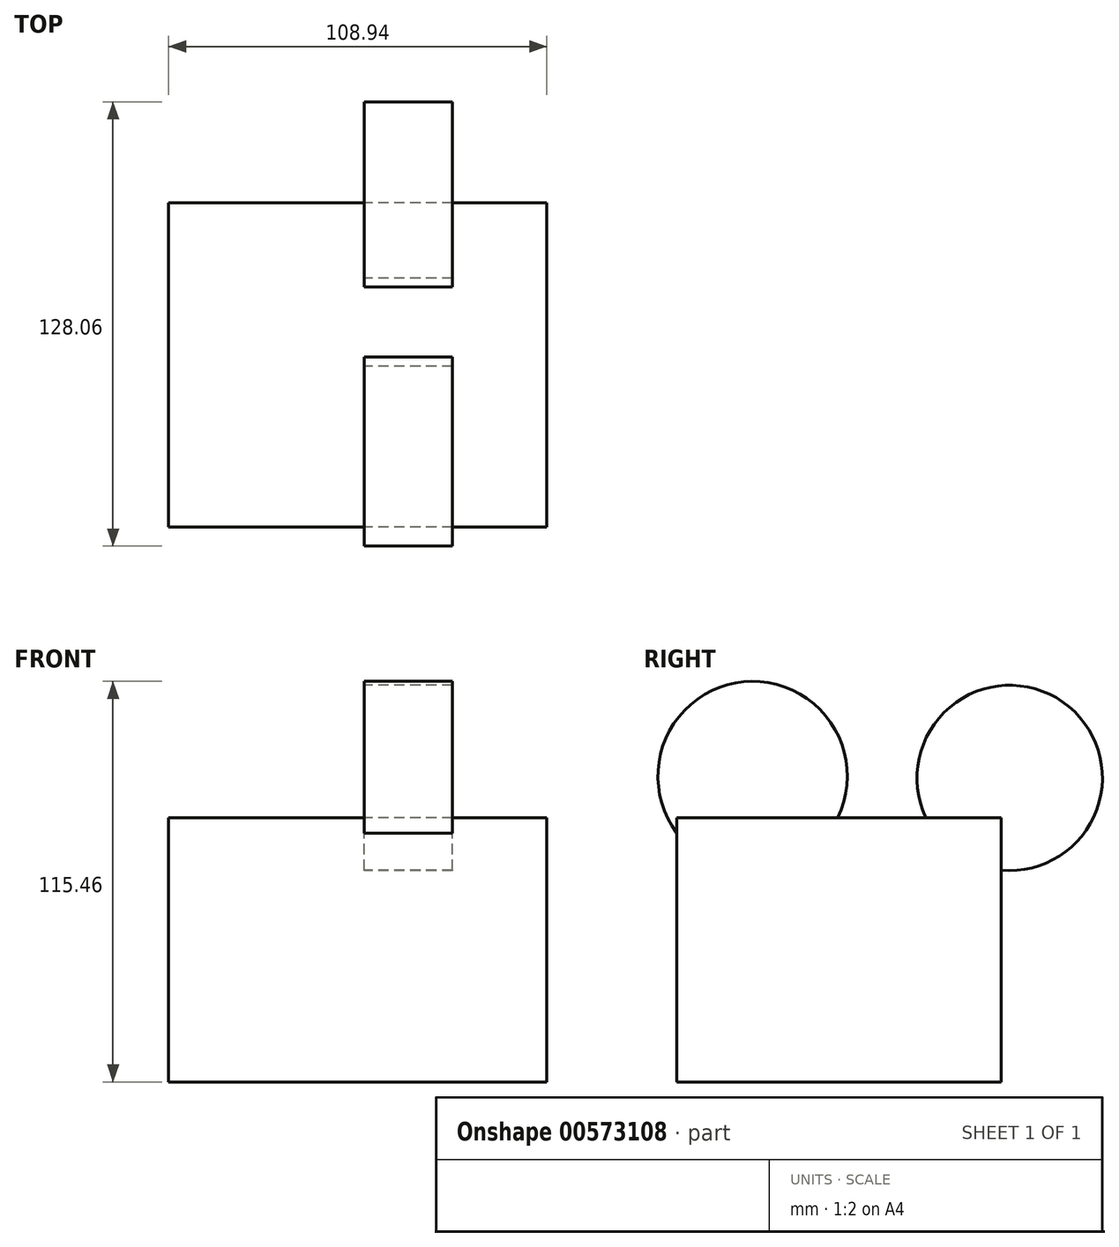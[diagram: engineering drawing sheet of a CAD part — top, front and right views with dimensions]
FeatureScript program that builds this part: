
annotation { "Feature Type Name" : "Feature", "Feature Type Description" : "" }
export const myFeature = defineFeature(function(context is Context, id is Id, definition is map)
    precondition{}
    {
        {
            var Q0;
            Q0=qCreatedBy(makeId("Top.planeOp"),FACE);
            var sketch = newSketch(context, id + "F0", { "sketchPlane" : qUnion([Q0])});
            skLineSegment(sketch, "E0.bottom", {"start": v(-51.08, 45.67) * mm, "end": v(59.45, 45.67) * mm});
            skLineSegment(sketch, "E0.top", {"start": v(-51.08, -51.44) * mm, "end": v(59.45, -51.44) * mm});
            skLineSegment(sketch, "E0.left", {"start": v(-51.08, 45.67) * mm, "end": v(-51.08, -51.44) * mm});
            skLineSegment(sketch, "E0.right", {"start": v(59.45, 45.67) * mm, "end": v(59.45, -51.44) * mm});
            skSolve(sketch);
        }
        {
            var Q0;
            Q0=makeQuery(id+"F0.imprint","IMPRINT",FACE,{"disambiguationData":[TD([[makeQuery(id+"F0.imprint","IMPRINT",EDGE,{"derivedFrom":sQuery(id+"F0.wireOp",EDGE,"E0.bottom")}),-1.0]])]});
            extrude(context, id + "F1", {"entities" : qUnion([Q0]), "oppositeDirection" : true, "depth" : 25.4 * mm, "offsetDistance" : 25.4 * mm});
        }
        {
            var Q0;
            Q0=makeQuery(id+"F1.opExtrude","CAP_FACE",FACE,{"disambiguationData":[OSD([sQuery(id+"F0.wireOp",EDGE,"E0.bottom"),sQuery(id+"F0.wireOp",EDGE,"E0.top"),sQuery(id+"F0.wireOp",EDGE,"E0.left"),sQuery(id+"F0.wireOp",EDGE,"E0.right")])],"isStart":false});
            extrude(context, id + "F2", {"entities" : qUnion([Q0]), "operationType" : NewBodyOperationType.REMOVE, "oppositeDirection" : true, "depth" : 25.4 * mm, "offsetDistance" : 25.4 * mm});
        }
        {
            var Q0;
            Q0=qCreatedBy(makeId("Top.planeOp"),FACE);
            var sketch = newSketch(context, id + "F3", { "sketchPlane" : qUnion([Q0])});
            skLineSegment(sketch, "E1.bottom", {"start": v(-56.36, 46.74) * mm, "end": v(52.58, 46.74) * mm});
            skLineSegment(sketch, "E1.top", {"start": v(-56.36, -46.73) * mm, "end": v(52.58, -46.73) * mm});
            skLineSegment(sketch, "E1.left", {"start": v(-56.36, 46.74) * mm, "end": v(-56.36, -46.73) * mm});
            skLineSegment(sketch, "E1.right", {"start": v(52.58, 46.74) * mm, "end": v(52.58, -46.73) * mm});
            skSolve(sketch);
        }
        {
            var Q0;
            Q0=makeQuery(id+"F3.imprint","IMPRINT",FACE,{"disambiguationData":[TD([[makeQuery(id+"F3.imprint","IMPRINT",EDGE,{"derivedFrom":sQuery(id+"F3.wireOp",EDGE,"E1.bottom")}),-1.0]])]});
            extrude(context, id + "F4", {"entities" : qUnion([Q0]), "oppositeDirection" : true, "depth" : 25.4 * mm, "offsetDistance" : 25.4 * mm});
        }
        {
            var Q0;
            Q0=makeQuery(id+"F4.opExtrude","CAP_FACE",FACE,{"disambiguationData":[OSD([sQuery(id+"F3.wireOp",EDGE,"E1.bottom"),sQuery(id+"F3.wireOp",EDGE,"E1.top"),sQuery(id+"F3.wireOp",EDGE,"E1.left"),sQuery(id+"F3.wireOp",EDGE,"E1.right")])],"isStart":false});
            extrude(context, id + "F5", {"entities" : qUnion([Q0]), "operationType" : NewBodyOperationType.ADD, "depth" : 25.4 * mm, "offsetDistance" : 25.4 * mm});
        }
        {
            var Q0;
            Q0=makeQuery(id+"F5.opExtrude","CAP_FACE",FACE,{"disambiguationData":[OSD([sQuery(id+"F3.wireOp",EDGE,"E1.bottom"),sQuery(id+"F3.wireOp",EDGE,"E1.top"),sQuery(id+"F3.wireOp",EDGE,"E1.left"),sQuery(id+"F3.wireOp",EDGE,"E1.right")])],"isStart":false});
            extrude(context, id + "F6", {"entities" : qUnion([Q0]), "operationType" : NewBodyOperationType.ADD, "depth" : 25.4 * mm, "offsetDistance" : 25.4 * mm});
        }
        {
            var Q0;
            Q0=qCreatedBy(makeId("Right.planeOp"),FACE);
            var sketch = newSketch(context, id + "F7", { "sketchPlane" : qUnion([Q0])});
            skCircle(sketch, "E2", {"center": v(49.13, 11.45) * mm, "radius": 26.7 * mm});
            skSolve(sketch);
        }
        {
            var Q0;
            Q0=makeQuery(id+"F7.imprint","IMPRINT",FACE,{"disambiguationData":[TD([[makeQuery(id+"F7.imprint","IMPRINT",EDGE,{"derivedFrom":sQuery(id+"F7.wireOp",EDGE,"E2")}),1.0]])]});
            extrude(context, id + "F8", {"entities" : qUnion([Q0]), "operationType" : NewBodyOperationType.ADD, "depth" : 25.4 * mm, "offsetDistance" : 25.4 * mm});
        }
        {
            var Q0;
            Q0=qCreatedBy(makeId("Right.planeOp"),FACE);
            var sketch = newSketch(context, id + "F9", { "sketchPlane" : qUnion([Q0])});
            skCircle(sketch, "E3", {"center": v(-24.94, 11.97) * mm, "radius": 27.3 * mm});
            skSolve(sketch);
        }
        {
            var Q0;
            Q0=makeQuery(id+"F9.imprint","IMPRINT",FACE,{"disambiguationData":[TD([[makeQuery(id+"F9.imprint","IMPRINT",EDGE,{"derivedFrom":sQuery(id+"F9.wireOp",EDGE,"E3")}),1.0]])]});
            extrude(context, id + "F10", {"entities" : qUnion([Q0]), "operationType" : NewBodyOperationType.ADD, "depth" : 25.4 * mm, "offsetDistance" : 25.4 * mm});
        }
    });
